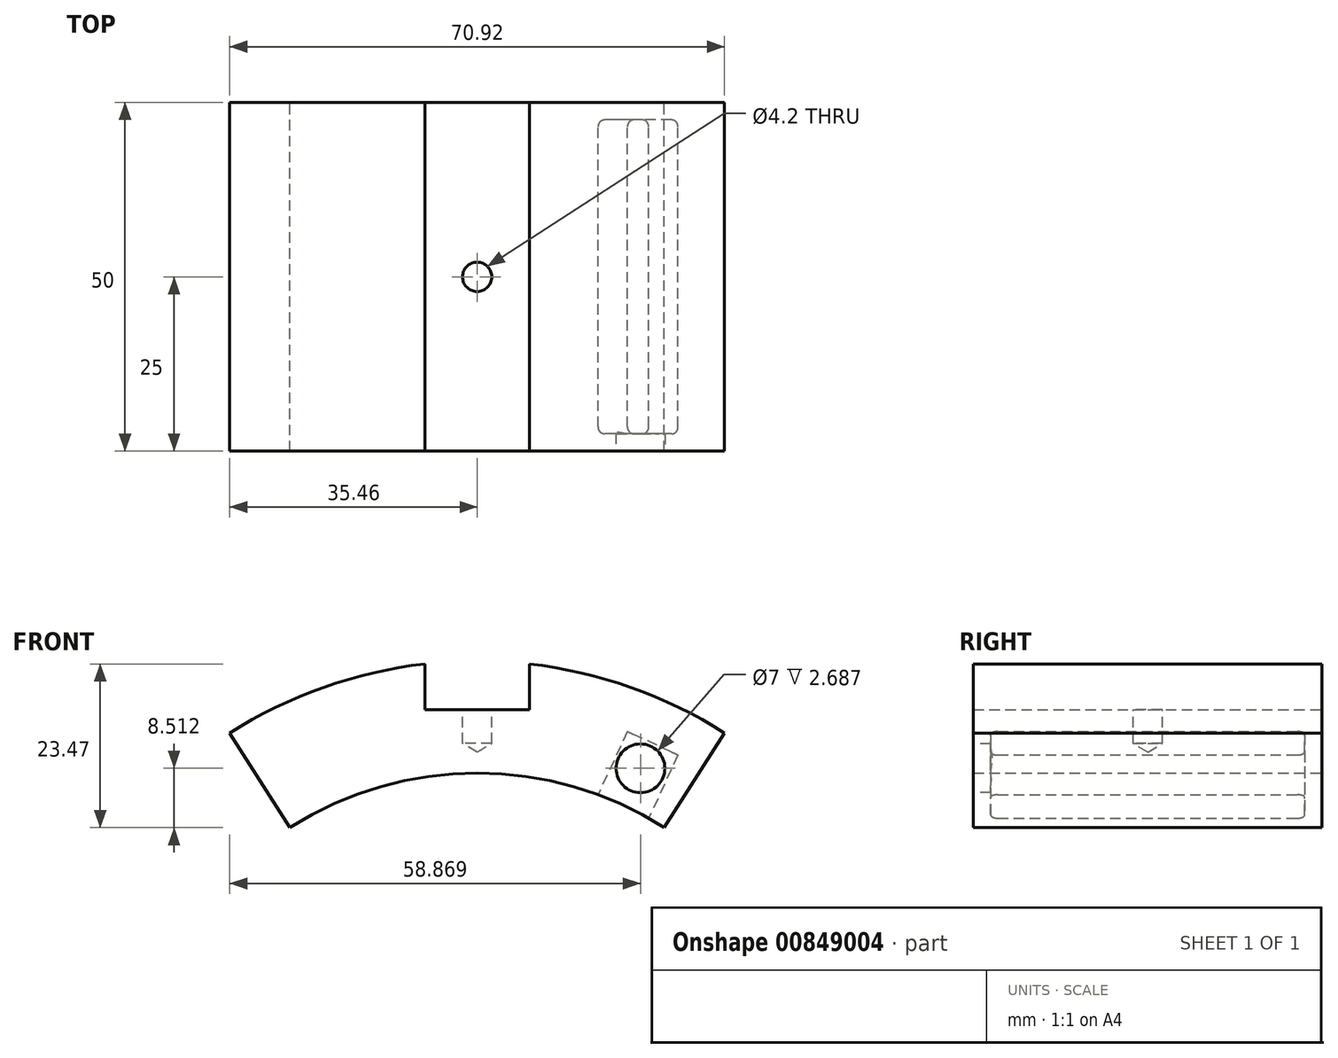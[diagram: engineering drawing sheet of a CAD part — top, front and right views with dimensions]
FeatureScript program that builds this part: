
annotation { "Feature Type Name" : "Feature", "Feature Type Description" : "" }
export const myFeature = defineFeature(function(context is Context, id is Id, definition is map)
    precondition{}
    {
        {
            assignVariable(context, id + "F0", {"name" : "largo_axial", "anyValue" : 50});
        }
        {
            assignVariable(context, id + "F1", {"name" : "profundidad_leg", "anyValue" : 10});
        }
        {
            var Q0;
            Q0=qCreatedBy(makeId("Front.planeOp"),FACE);
            var sketch = newSketch(context, id + "F2", { "sketchPlane" : qUnion([Q0])});
            skArc(sketch, "E0", {"start": v(26.82, 42.1) * mm, "mid": v(0, 49.92) * mm, "end": v(-26.82, 42.1) * mm});
            skLineSegment(sketch, "E1", {"start": v(0, 0) * mm, "end": v(26.82, 42.1) * mm});
            skLineSegment(sketch, "E2", {"start": v(0, 0) * mm, "end": v(-26.82, 42.1) * mm});
            skLineSegment(sketch, "E3", {"start": v(0, 0) * mm, "end": v(35.46, 55.66) * mm});
            skLineSegment(sketch, "E4", {"start": v(0, 0) * mm, "end": v(-35.46, 55.66) * mm});
            skArc(sketch, "E5", {"start": v(35.46, 55.66) * mm, "mid": v(0, 66) * mm, "end": v(-35.46, 55.66) * mm});
            skLineSegment(sketch, "E6", {"start": v(0, 49.92) * mm, "end": v(0, 59) * mm});
            skLineSegment(sketch, "E7", {"start": v(0, 59) * mm, "end": v(-7.5, 59) * mm});
            skLineSegment(sketch, "E8", {"start": v(-7.5, 59) * mm, "end": v(-7.5, 65.57) * mm});
            skLineSegment(sketch, "E9.MirrorCS", {"start": v(0, 59) * mm, "end": v(7.5, 59) * mm});
            skLineSegment(sketch, "E10.MirrorCS", {"start": v(7.5, 59) * mm, "end": v(7.5, 65.57) * mm});
            skSolve(sketch);
        }
        {
            var Q0;
            {var subQ0=sQuery(id+"F2.wireOp",EDGE,"E6");Q0=makeQuery(id+"F2.imprint","IMPRINT",FACE,{"disambiguationData":[TD([[makeQuery(id+"F2.imprint","IMPRINT",EDGE,{"derivedFrom":subQ0}),1.0]])]});}
            var Q1;
            {var subQ0=sQuery(id+"F2.wireOp",EDGE,"E6");Q1=makeQuery(id+"F2.imprint","IMPRINT",FACE,{"disambiguationData":[TD([[makeQuery(id+"F2.imprint","IMPRINT",EDGE,{"derivedFrom":subQ0}),-1.0]])]});}
            extrude(context, id + "F3", {"entities" : qUnion([Q0, Q1]), "depth" : (getVariable(context, 'largo_axial')) * mm, "offsetDistance" : 25 * mm});
        }
        {
            var Q0;
            Q0=makeQuery(id+"F3.opExtrude","CAP_FACE",FACE,{"disambiguationData":[OSD([sQuery(id+"F2.wireOp",EDGE,"E0"),sQuery(id+"F2.wireOp",EDGE,"E3"),sQuery(id+"F2.wireOp",EDGE,"E4"),sQuery(id+"F2.wireOp",EDGE,"E5"),sQuery(id+"F2.wireOp",EDGE,"E7"),sQuery(id+"F2.wireOp",EDGE,"E8"),sQuery(id+"F2.wireOp",EDGE,"E9.MirrorCS"),sQuery(id+"F2.wireOp",EDGE,"E10.MirrorCS")])],"isStart":false});
            var sketch = newSketch(context, id + "F4", { "sketchPlane" : qUnion([Q0])});
            skLineSegment(sketch, "E11", {"start": v(0, 0) * mm, "end": v(24.58, 43.45) * mm});
            skLineSegment(sketch, "E12", {"start": v(24.58, 43.45) * mm, "end": v(17.33, 46.82) * mm});
            skSolve(sketch);
        }
        {
            var Q0;
            Q0=sQuery(id+"F4.wireOp",EDGE,"E12");
            cPlane(context, id + "F5", {"entities" : qUnion([Q0]), "cplaneType" : CPlaneType.LINE_ANGLE, "offset" : 25 * mm, "angle" : 90 * degree, "width" : 150 * mm, "height" : 150 * mm});
        }
        {
            var Q0;
            Q0=qCreatedBy(id+"F5.planeOp",FACE);
            var sketch = newSketch(context, id + "F6", { "sketchPlane" : qUnion([Q0])});
            skLineSegment(sketch, "E13.0", {"start": v(4, -50) * mm, "end": v(-4, -50) * mm});
            skLineSegment(sketch, "E14", {"start": v(4, -46.5) * mm, "end": v(4, -3.5) * mm});
            skLineSegment(sketch, "E15", {"start": v(-4, -46.5) * mm, "end": v(-4, -3.5) * mm});
            skPoint(sketch, "E16", {"position": v(4, -47.5) * mm});
            skPoint(sketch, "E17", {"position": v(6, -2.5) * mm});
            skPoint(sketch, "E18", {"position": v(4, -5) * mm});
            skLineSegment(sketch, "E19", {"start": v(3, -47.5) * mm, "end": v(-3, -47.5) * mm});
            skLineSegment(sketch, "E20", {"start": v(3, -2.5) * mm, "end": v(-3, -2.5) * mm});
            skArc(sketch, "E21.filletArc", {"start": v(-4, -46.5) * mm, "mid": v(-3.7, -47.2) * mm, "end": v(-3, -47.5) * mm});
            skPoint(sketch, "E22.newPointA", {"position": v(-4, 0) * mm});
            skArc(sketch, "E22.filletArc", {"start": v(-3, -2.5) * mm, "mid": v(-3.7, -2.8) * mm, "end": v(-4, -3.5) * mm});
            skPoint(sketch, "E23.newPointB", {"position": v(4, 0) * mm});
            skArc(sketch, "E23.filletArc", {"start": v(4, -3.5) * mm, "mid": v(3.7, -2.8) * mm, "end": v(3, -2.5) * mm});
            skArc(sketch, "E24.filletArc", {"start": v(3, -47.5) * mm, "mid": v(3.7, -47.2) * mm, "end": v(4, -46.5) * mm});
            skSolve(sketch);
        }
        {
            var Q0;
            Q0=makeQuery(id+"F6.imprint","IMPRINT",FACE,{"disambiguationData":[TD([[makeQuery(id+"F6.imprint","IMPRINT",EDGE,{"derivedFrom":sQuery(id+"F6.wireOp",EDGE,"E14")}),1.0]])]});
            extrude(context, id + "F7", {"entities" : qUnion([Q0]), "operationType" : NewBodyOperationType.REMOVE, "depth" : (getVariable(context, 'profundidad_leg')) * mm, "offsetDistance" : 25 * mm});
        }
        {
            var Q0;
            Q0=makeQuery(id+"F3.opExtrude","SWEPT_FACE",FACE,{"disambiguationData":[OSD([sQuery(id+"F2.wireOp",EDGE,"E7"),sQuery(id+"F2.wireOp",EDGE,"E9.MirrorCS")])]});
            var sketch = newSketch(context, id + "F8", { "sketchPlane" : qUnion([Q0])});
            skLineSegment(sketch, "E25", {"start": v(0, 0) * mm, "end": v(0, -50) * mm});
            skPoint(sketch, "E26", {"position": v(0, -25) * mm});
            skSolve(sketch);
        }
        {
            var Q0;
            Q0=sQuery(id+"F8.wireOp",VERTEX,"E26");
            var Q1;
            Q1=makeQuery(id+"F3.opExtrude","SWEPT_BODY",BODY,{"disambiguationData":[OSD([sQuery(id+"F2.wireOp",EDGE,"E0"),sQuery(id+"F2.wireOp",EDGE,"E3"),sQuery(id+"F2.wireOp",EDGE,"E4"),sQuery(id+"F2.wireOp",EDGE,"E5"),sQuery(id+"F2.wireOp",EDGE,"E7"),sQuery(id+"F2.wireOp",EDGE,"E8"),sQuery(id+"F2.wireOp",EDGE,"E9.MirrorCS"),sQuery(id+"F2.wireOp",EDGE,"E10.MirrorCS")])]});
            hole(context, id + "F9", {"style" : HoleStyle.SIMPLE, "endStyle" : HoleEndStyle.BLIND, "standardTappedOrClearance" : lookupTablePath({ "standard" : "ISO", "engagement" : "75%", "pitch" : "0.8 mm", "size" : "M5", "type" : "Tapped" }), "standardBlindInLast" : lookupTablePath({ "standard" : "ISO", "engagement" : "75%", "pitch" : "0.8 mm", "size" : "M5", "type" : "Tapped" }), "holeDiameter" : 4.2 * mm, "majorDiameter" : 5 * mm, "showTappedDepth" : true, "holeDepth" : 4.8 * mm, "isTappedThrough" : true, "tappedDepth" : 4 * mm, "tapClearance" : 1, "startFromSketch" : true, "locations" : qUnion([Q0]), "scope" : qUnion([Q1])});
        }
        {
            var Q0;
            {var subQ3=sQuery(id+"F2.wireOp",EDGE,"E3");var subQ6=makeQuery(id+"F3.opExtrude","CAP_EDGE",EDGE,{"disambiguationData":[OSD([subQ3])],"isStart":false});Q0=makeQuery(id+"F4.imprint","IMPRINT",FACE,{"disambiguationData":[TD([[makeQuery(id+"F4.imprint","IMPRINT",EDGE,{"derivedFrom":subQ6}),1.0]])]});}
            var sketch = newSketch(context, id + "F10", { "sketchPlane" : qUnion([Q0])});
            skLineSegment(sketch, "E27.0", {"start": v(24.58, 43.45) * mm, "end": v(17.33, 46.82) * mm});
            skLineSegment(sketch, "E28", {"start": v(24.58, 43.45) * mm, "end": v(28.8, 52.52) * mm});
            skLineSegment(sketch, "E29", {"start": v(28.8, 52.52) * mm, "end": v(21.6, 56.03) * mm});
            skLineSegment(sketch, "E30", {"start": v(21.6, 56.03) * mm, "end": v(17.33, 46.82) * mm});
            skPoint(sketch, "E31", {"position": v(25.17, 54.2) * mm});
            skLineSegment(sketch, "E32", {"start": v(25.17, 54.2) * mm, "end": v(23.4, 50.61) * mm});
            skSolve(sketch);
        }
        {
            var Q0;
            Q0=sQuery(id+"F10.wireOp",VERTEX,"E32.end");
            var Q1;
            Q1=makeQuery(id+"F3.opExtrude","SWEPT_BODY",BODY,{"disambiguationData":[OSD([sQuery(id+"F2.wireOp",EDGE,"E0"),sQuery(id+"F2.wireOp",EDGE,"E3"),sQuery(id+"F2.wireOp",EDGE,"E4"),sQuery(id+"F2.wireOp",EDGE,"E5"),sQuery(id+"F2.wireOp",EDGE,"E7"),sQuery(id+"F2.wireOp",EDGE,"E8"),sQuery(id+"F2.wireOp",EDGE,"E9.MirrorCS"),sQuery(id+"F2.wireOp",EDGE,"E10.MirrorCS")])]});
            hole(context, id + "F11", {"style" : HoleStyle.SIMPLE, "endStyle" : HoleEndStyle.BLIND, "standardTappedOrClearance" : lookupTablePath({ "standard" : "ISO", "engagement" : "75%", "pitch" : "1 mm", "size" : "M8", "type" : "Tapped" }), "standardBlindInLast" : lookupTablePath({ "standard" : "ISO", "engagement" : "75%", "pitch" : "1 mm", "size" : "M8", "type" : "Tapped" }), "holeDiameter" : 7 * mm, "majorDiameter" : 8 * mm, "showTappedDepth" : true, "holeDepth" : 28 * mm, "tappedDepth" : 0.5 * (getVariable(context, 'largo_axial')) * mm, "tapClearance" : 3, "startFromSketch" : true, "locations" : qUnion([Q0]), "scope" : qUnion([Q1])});
        }
    });
